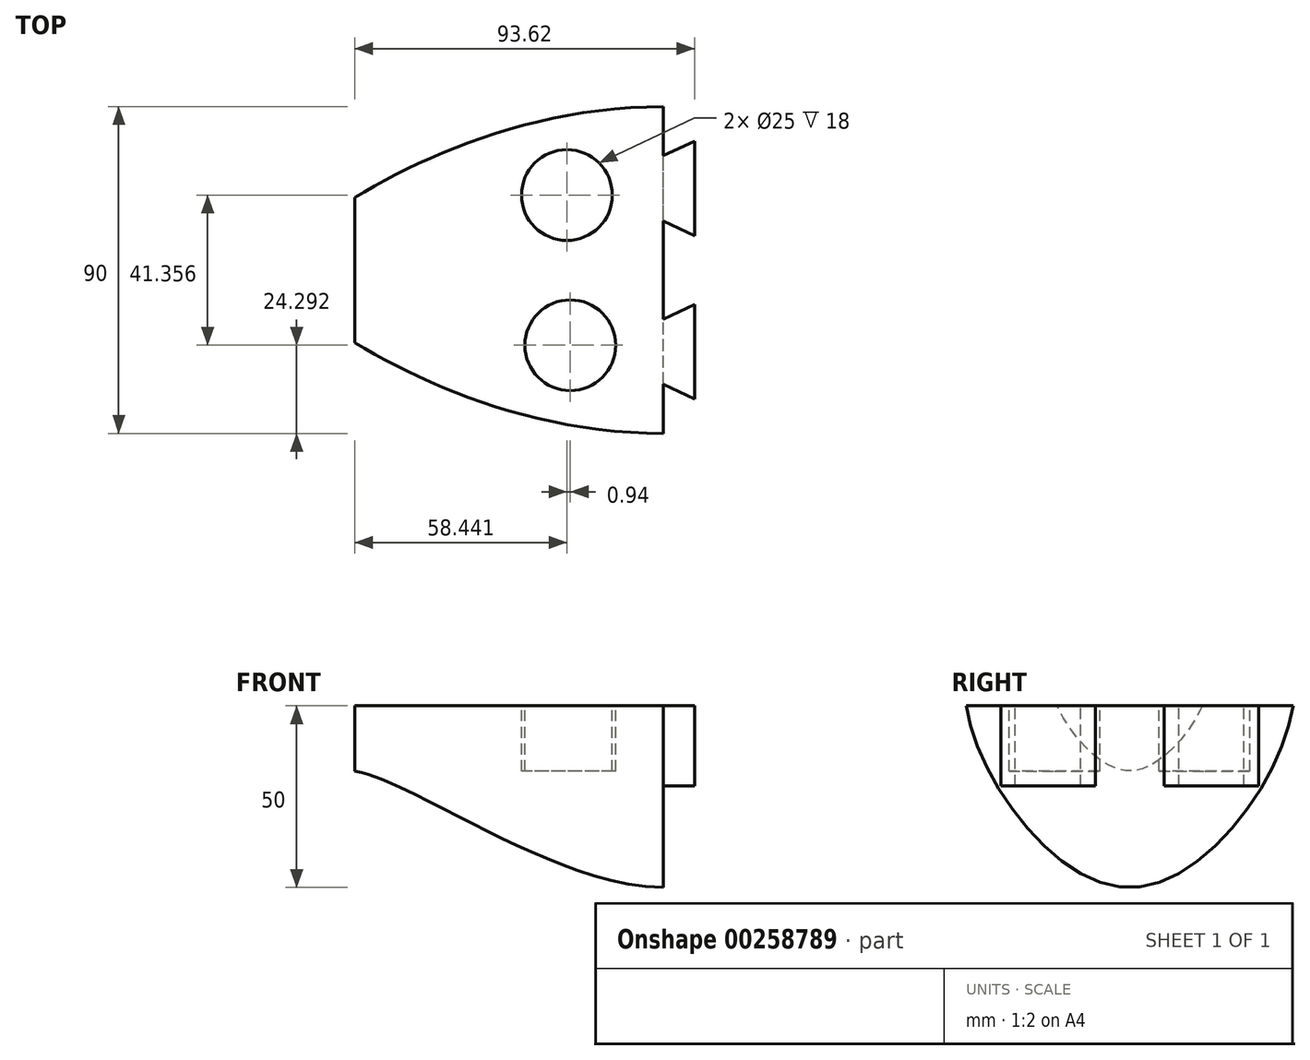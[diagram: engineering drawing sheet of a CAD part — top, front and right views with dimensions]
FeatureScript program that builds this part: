
annotation { "Feature Type Name" : "Feature", "Feature Type Description" : "" }
export const myFeature = defineFeature(function(context is Context, id is Id, definition is map)
    precondition{}
    {
        {
            var Q0;
            Q0=qCreatedBy(makeId("Right.planeOp"),FACE);
            cPlane(context, id + "F0", {"entities" : qUnion([Q0]), "cplaneType" : CPlaneType.OFFSET, "offset" : 85 * mm, "oppositeDirection" : true, "width" : 150 * mm, "height" : 150 * mm});
        }
        {
            var Q0;
            Q0=qCreatedBy(makeId("Right.planeOp"),FACE);
            var sketch = newSketch(context, id + "F1", { "sketchPlane" : qUnion([Q0])});
            skFitSpline(sketch, "E0", {"points": [v(-45, 0) * mm, v(0, -50) * mm, v(45, 0) * mm], "startDerivative": vector(18, -120) * mm, "endDerivative": vector(18, 120) * mm});
            skLineSegment(sketch, "E1", {"start": v(-45, 0) * mm, "end": v(45, 0) * mm});
            skSolve(sketch);
        }
        {
            var Q0;
            Q0=qCreatedBy(id+"F0.planeOp",FACE);
            var sketch = newSketch(context, id + "F2", { "sketchPlane" : qUnion([Q0])});
            skFitSpline(sketch, "E2", {"points": [v(20, 0) * mm, v(0, -18) * mm, v(-20, 0) * mm], "startDerivative": vector(-12, -30) * mm, "endDerivative": vector(-12, 30) * mm});
            skLineSegment(sketch, "E3", {"start": v(20, 0) * mm, "end": v(-20, 0) * mm});
            skSolve(sketch);
        }
        {
            var Q0;
            Q0=qCreatedBy(makeId("Top.planeOp"),FACE);
            var sketch = newSketch(context, id + "F3", { "sketchPlane" : qUnion([Q0])});
            skFitSpline(sketch, "E4", {"points": [v(-85, 20) * mm, v(0, 45) * mm], "startDerivative": vector(60, 36) * mm, "endDerivative": vector(105, 0) * mm});
            skSolve(sketch);
        }
        {
            var Q0;
            Q0=qCreatedBy(makeId("Top.planeOp"),FACE);
            var sketch = newSketch(context, id + "F4", { "sketchPlane" : qUnion([Q0])});
            skFitSpline(sketch, "E5", {"points": [v(-85, -20) * mm, v(0, -45) * mm], "startDerivative": vector(60, -36) * mm, "endDerivative": vector(105, 0) * mm});
            skSolve(sketch);
        }
        {
            var Q0;
            Q0=qCreatedBy(makeId("Front.planeOp"),FACE);
            var sketch = newSketch(context, id + "F5", { "sketchPlane" : qUnion([Q0])});
            skFitSpline(sketch, "E6", {"points": [v(-85, -18) * mm, v(0, -50) * mm], "startDerivative": vector(45, -6) * mm, "endDerivative": vector(89.2, 0) * mm});
            skSolve(sketch);
        }
        {
            var Q0;
            Q0=makeQuery(id+"F1.imprint","IMPRINT",FACE,{"disambiguationData":[TD([[makeQuery(id+"F1.imprint","IMPRINT",EDGE,{"derivedFrom":sQuery(id+"F1.wireOp",EDGE,"E0")}),1.0]])]});
            var Q1;
            Q1=makeQuery(id+"F2.imprint","IMPRINT",FACE,{"disambiguationData":[TD([[makeQuery(id+"F2.imprint","IMPRINT",EDGE,{"derivedFrom":sQuery(id+"F2.wireOp",EDGE,"E2")}),-1.0]])]});
            var Q2;
            Q2=sQuery(id+"F3.wireOp",EDGE,"E4");
            var Q3;
            Q3=sQuery(id+"F4.wireOp",EDGE,"E5");
            var Q4;
            Q4=sQuery(id+"F5.wireOp",EDGE,"E6");
            loft(context, id + "F6", {"addGuides" : true, "sheetProfilesArray" : [{ "sheetProfileEntities" : qUnion([Q0]) }, { "sheetProfileEntities" : qUnion([Q1]) }], "guidesArray" : [{ "guideEntities" : qUnion([Q2]), "guideDerivativeType" : LoftGuideDerivativeType.DEFAULT, "guideDerivativeMagnitude" : 1 }, { "guideEntities" : qUnion([Q3]), "guideDerivativeType" : LoftGuideDerivativeType.DEFAULT, "guideDerivativeMagnitude" : 1 }, { "guideEntities" : qUnion([Q4]), "guideDerivativeType" : LoftGuideDerivativeType.DEFAULT, "guideDerivativeMagnitude" : 1 }]});
        }
        {
            var Q0;
            Q0=makeQuery(id+"F6.opLoft","SWEPT_FACE",FACE,{"disambiguationData":[OSD([sQuery(id+"F1.wireOp",EDGE,"E1"),sQuery(id+"F2.wireOp",EDGE,"E2"),sQuery(id+"F2.wireOp",EDGE,"E3"),sQuery(id+"F3.wireOp",EDGE,"E4"),sQuery(id+"F4.wireOp",EDGE,"E5")])]});
            var sketch = newSketch(context, id + "F7", { "sketchPlane" : qUnion([Q0])});
            skLineSegment(sketch, "E7", {"start": v(0, -31.5) * mm, "end": v(8.62, -35.5) * mm});
            skLineSegment(sketch, "E8", {"start": v(8.62, -35.5) * mm, "end": v(8.62, -9.5) * mm});
            skLineSegment(sketch, "E9", {"start": v(8.62, -9.5) * mm, "end": v(0, -13.5) * mm});
            skSolve(sketch);
        }
        {
            var Q0;
            {var subQ0=sQuery(id+"F7.wireOp",EDGE,"E7");Q0=makeQuery(id+"F7.imprint","IMPRINT",FACE,{"disambiguationData":[TD([[makeQuery(id+"F7.imprint","IMPRINT",EDGE,{"derivedFrom":subQ0}),1.0]])]});}
            extrude(context, id + "F8", {"entities" : qUnion([Q0]), "operationType" : NewBodyOperationType.ADD, "oppositeDirection" : true, "depth" : 22 * mm});
        }
        {
            var Q0;
            {var subQ0=sQuery(id+"F4.wireOp",EDGE,"E5");var subQ1=sQuery(id+"F3.wireOp",EDGE,"E4");var subQ2=sQuery(id+"F1.wireOp",EDGE,"E1");Q0=makeQuery(id+"F8.boolean.opBoolean","MERGE",FACE,{"derivedFrom":[makeQuery(id+"F6.opLoft","SWEPT_FACE",FACE,{"disambiguationData":[OSD([subQ2,sQuery(id+"F2.wireOp",EDGE,"E2"),sQuery(id+"F2.wireOp",EDGE,"E3"),subQ1,subQ0])]}),makeQuery(id+"F8.opExtrude","CAP_FACE",FACE,{"disambiguationData":[OSD([subQ2,subQ1,subQ0,sQuery(id+"F7.wireOp",EDGE,"E7"),sQuery(id+"F7.wireOp",EDGE,"E8"),sQuery(id+"F7.wireOp",EDGE,"E9")])],"isStart":true})]});}
            var sketch = newSketch(context, id + "F9", { "sketchPlane" : qUnion([Q0])});
            skLineSegment(sketch, "E10", {"start": v(8.62, 9.5) * mm, "end": v(8.62, 35.5) * mm});
            skLineSegment(sketch, "E11", {"start": v(8.62, 35.5) * mm, "end": v(0, 31.5) * mm});
            skLineSegment(sketch, "E12", {"start": v(0, 13.5) * mm, "end": v(8.62, 9.5) * mm});
            skSolve(sketch);
        }
        {
            var Q0;
            Q0=makeQuery(id+"F9.imprint","IMPRINT",FACE,{"disambiguationData":[TD([[makeQuery(id+"F9.imprint","IMPRINT",EDGE,{"derivedFrom":sQuery(id+"F9.wireOp",EDGE,"E10")}),1.0]])]});
            extrude(context, id + "F10", {"entities" : qUnion([Q0]), "operationType" : NewBodyOperationType.ADD, "oppositeDirection" : true, "depth" : 22 * mm});
        }
        {
            var Q0;
            {var subQ0=sQuery(id+"F4.wireOp",EDGE,"E5");var subQ1=sQuery(id+"F3.wireOp",EDGE,"E4");var subQ2=sQuery(id+"F1.wireOp",EDGE,"E1");Q0=makeQuery(id+"F10.boolean.opBoolean","MERGE",FACE,{"derivedFrom":[makeQuery(id+"F8.boolean.opBoolean","MERGE",FACE,{"derivedFrom":[makeQuery(id+"F6.opLoft","SWEPT_FACE",FACE,{"disambiguationData":[OSD([subQ2,sQuery(id+"F2.wireOp",EDGE,"E2"),sQuery(id+"F2.wireOp",EDGE,"E3"),subQ1,subQ0])]}),makeQuery(id+"F8.opExtrude","CAP_FACE",FACE,{"disambiguationData":[OSD([subQ2,subQ1,subQ0,sQuery(id+"F7.wireOp",EDGE,"E7"),sQuery(id+"F7.wireOp",EDGE,"E8"),sQuery(id+"F7.wireOp",EDGE,"E9")])],"isStart":true})]}),makeQuery(id+"F10.opExtrude","CAP_FACE",FACE,{"disambiguationData":[OSD([subQ2,subQ1,subQ0,sQuery(id+"F9.wireOp",EDGE,"E10"),sQuery(id+"F9.wireOp",EDGE,"E11"),sQuery(id+"F9.wireOp",EDGE,"E12")])],"isStart":true})]});}
            var sketch = newSketch(context, id + "F11", { "sketchPlane" : qUnion([Q0])});
            skCircle(sketch, "E13", {"center": v(-25.62, -20.7) * mm, "radius": 12.5 * mm});
            skCircle(sketch, "E14", {"center": v(-26.56, 20.65) * mm, "radius": 12.5 * mm});
            skSolve(sketch);
        }
        {
            var Q0;
            Q0=makeQuery(id+"F11.imprint","IMPRINT",FACE,{"disambiguationData":[TD([[makeQuery(id+"F11.imprint","IMPRINT",EDGE,{"derivedFrom":sQuery(id+"F11.wireOp",EDGE,"E13")}),1.0]])]});
            var Q1;
            Q1=makeQuery(id+"F11.imprint","IMPRINT",FACE,{"disambiguationData":[TD([[makeQuery(id+"F11.imprint","IMPRINT",EDGE,{"derivedFrom":sQuery(id+"F11.wireOp",EDGE,"E14")}),1.0]])]});
            extrude(context, id + "F12", {"entities" : qUnion([Q0, Q1]), "operationType" : NewBodyOperationType.REMOVE, "oppositeDirection" : true, "depth" : 18 * mm});
        }
    });
